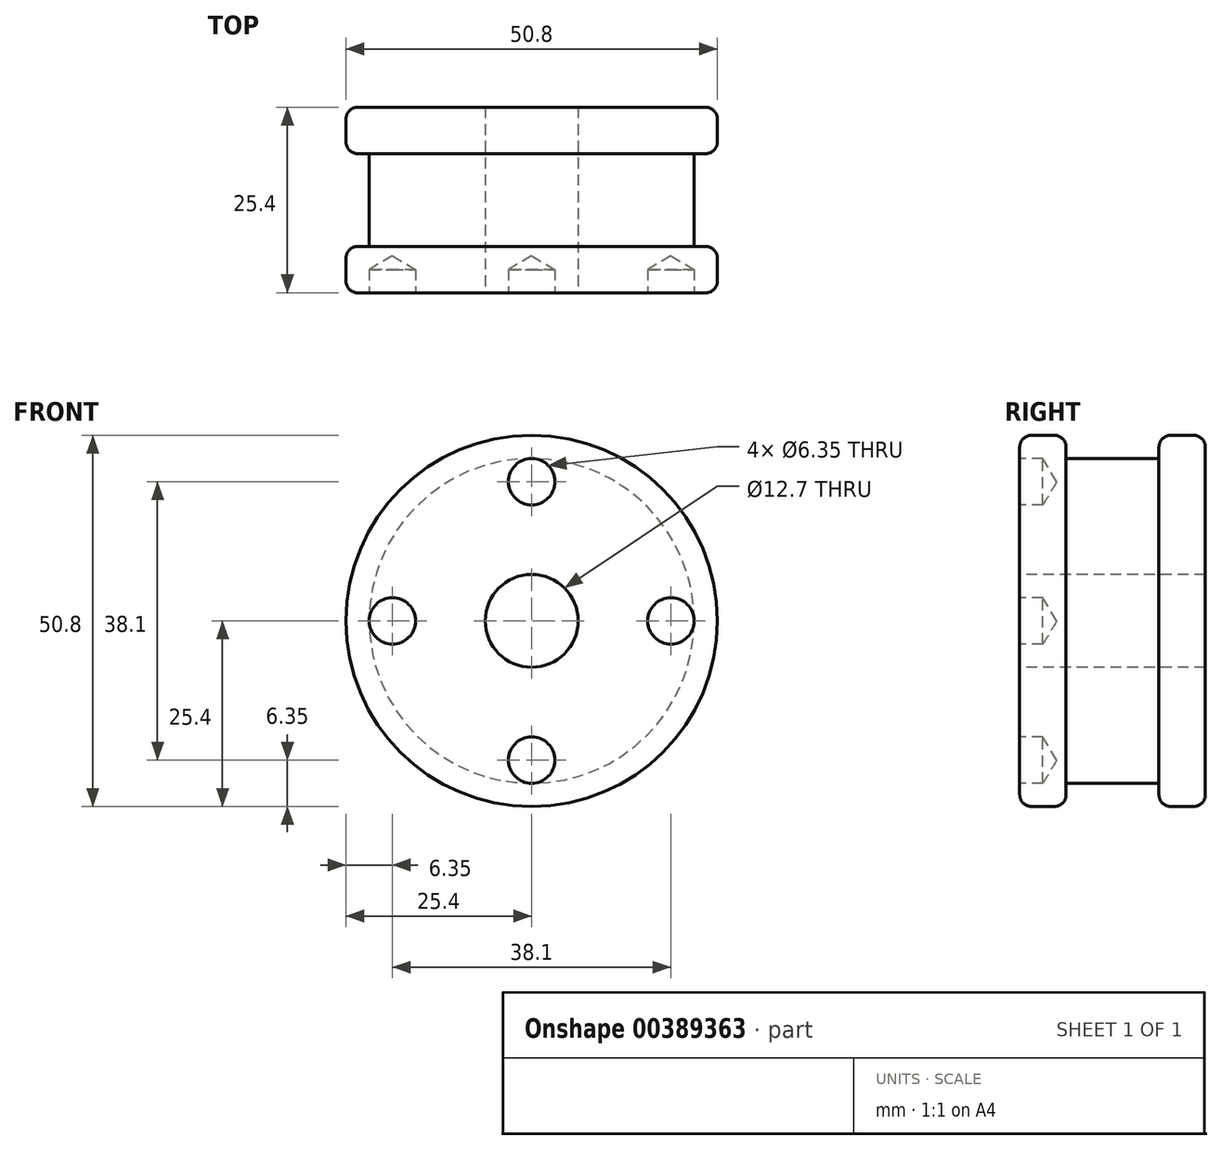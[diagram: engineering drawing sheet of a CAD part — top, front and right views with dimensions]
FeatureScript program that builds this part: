
annotation { "Feature Type Name" : "Feature", "Feature Type Description" : "" }
export const myFeature = defineFeature(function(context is Context, id is Id, definition is map)
    precondition{}
    {
        {
            var Q0;
            Q0=qCreatedBy(makeId("Front.planeOp"),FACE);
            var sketch = newSketch(context, id + "F0", { "sketchPlane" : qUnion([Q0])});
            skCircle(sketch, "E0", {"center": v(0, 0) * mm, "radius": 25.4 * mm});
            skSolve(sketch);
        }
        {
            var Q0;
            Q0 = qSketchRegion(id + "F0", true);
            extrude(context, id + "F1", {"entities" : qUnion([Q0]), "depth" : 6.35 * mm});
        }
        {
            var Q0;
            Q0=makeQuery(id+"F1.opExtrude","CAP_FACE",FACE,{"disambiguationData":[OSD([sQuery(id+"F0.wireOp",EDGE,"E0")])],"isStart":false});
            var sketch = newSketch(context, id + "F2", { "sketchPlane" : qUnion([Q0])});
            skCircle(sketch, "E1", {"center": v(0, 0) * mm, "radius": 22.23 * mm});
            skSolve(sketch);
        }
        {
            var Q0;
            Q0 = qSketchRegion(id + "F2", true);
            extrude(context, id + "F3", {"entities" : qUnion([Q0]), "operationType" : NewBodyOperationType.ADD, "depth" : 12.7 * mm});
        }
        {
            var Q0;
            Q0=makeQuery(id+"F3.opExtrude","CAP_FACE",FACE,{"disambiguationData":[OSD([sQuery(id+"F2.wireOp",EDGE,"E1")])],"isStart":false});
            var sketch = newSketch(context, id + "F4", { "sketchPlane" : qUnion([Q0])});
            skCircle(sketch, "E2", {"center": v(0, 0) * mm, "radius": 25.4 * mm});
            skSolve(sketch);
        }
        {
            var Q0;
            Q0 = qSketchRegion(id + "F4", true);
            extrude(context, id + "F5", {"entities" : qUnion([Q0]), "operationType" : NewBodyOperationType.ADD, "depth" : 6.35 * mm});
        }
        {
            var Q0;
            Q0=makeQuery(id+"F5.opExtrude","CAP_FACE",FACE,{"disambiguationData":[OSD([sQuery(id+"F4.wireOp",EDGE,"E2")])],"isStart":false});
            var sketch = newSketch(context, id + "F6", { "sketchPlane" : qUnion([Q0])});
            skCircle(sketch, "E3", {"center": v(0, 19.05) * mm, "radius": 1.59 * mm});
            skCircle(sketch, "E4", {"center": v(19.05, 0) * mm, "radius": 1.59 * mm});
            skLineSegment(sketch, "E5", {"start": v(0, 25.4) * mm, "end": v(0, -25.4) * mm, "construction": true});
            skCircle(sketch, "E6", {"center": v(0, -19.05) * mm, "radius": 1.59 * mm});
            skCircle(sketch, "E7", {"center": v(-19.05, 0) * mm, "radius": 1.59 * mm});
            skCircle(sketch, "E8", {"center": v(0, 0) * mm, "radius": 6.35 * mm});
            skSolve(sketch);
        }
        {
            var Q0;
            Q0=sQuery(id+"F6.wireOp",VERTEX,"E3.center");
            var Q1;
            Q1=sQuery(id+"F6.wireOp",VERTEX,"E4.center");
            var Q2;
            Q2=sQuery(id+"F6.wireOp",VERTEX,"E6.center");
            var Q3;
            Q3=sQuery(id+"F6.wireOp",VERTEX,"E7.center");
            var Q4;
            Q4=makeQuery(id+"F1.opExtrude","SWEPT_BODY",BODY,{"disambiguationData":[OSD([sQuery(id+"F0.wireOp",EDGE,"E0")])]});
            hole(context, id + "F7", {"style" : HoleStyle.SIMPLE, "endStyle" : HoleEndStyle.BLIND, "holeDiameter" : 6.35 * mm, "holeDepth" : 3.17 * mm, "isTappedThrough" : true, "tappedDepth" : 12.7 * mm, "tapClearance" : 3, "locations" : qUnion([Q0, Q1, Q2, Q3]), "scope" : qUnion([Q4])});
        }
        {
            var Q0;
            Q0=makeQuery(id+"F5.opExtrude","CAP_EDGE",EDGE,{"disambiguationData":[OSD([sQuery(id+"F4.wireOp",EDGE,"E2")])],"isStart":false});
            var Q1;
            Q1=makeQuery(id+"F5.opExtrude","CAP_EDGE",EDGE,{"disambiguationData":[OSD([sQuery(id+"F4.wireOp",EDGE,"E2")])],"isStart":true});
            var Q2;
            Q2=makeQuery(id+"F1.opExtrude","CAP_EDGE",EDGE,{"disambiguationData":[OSD([sQuery(id+"F0.wireOp",EDGE,"E0")])],"isStart":false});
            var Q3;
            Q3=makeQuery(id+"F1.opExtrude","CAP_EDGE",EDGE,{"disambiguationData":[OSD([sQuery(id+"F0.wireOp",EDGE,"E0")])],"isStart":true});
            fillet(context, id + "F8", {"entities" : qUnion([Q0, Q1, Q2, Q3]), "radius" : 1.6 * mm, "tangentPropagation" : true, "allowEdgeOverflow" : false});
        }
        {
            var Q0;
            Q0=makeQuery(id+"F5.opExtrude","CAP_FACE",FACE,{"disambiguationData":[OSD([sQuery(id+"F4.wireOp",EDGE,"E2")])],"isStart":false});
            var sketch = newSketch(context, id + "F9", { "sketchPlane" : qUnion([Q0])});
            skCircle(sketch, "E9", {"center": v(0, 0) * mm, "radius": 6.35 * mm});
            skSolve(sketch);
        }
        {
            var Q0;
            Q0 = qSketchRegion(id + "F9", true);
            extrude(context, id + "F10", {"entities" : qUnion([Q0]), "operationType" : NewBodyOperationType.REMOVE, "endBound" : BoundingType.THROUGH_ALL, "oppositeDirection" : true, "depth" : 12.7 * mm});
        }
    });
